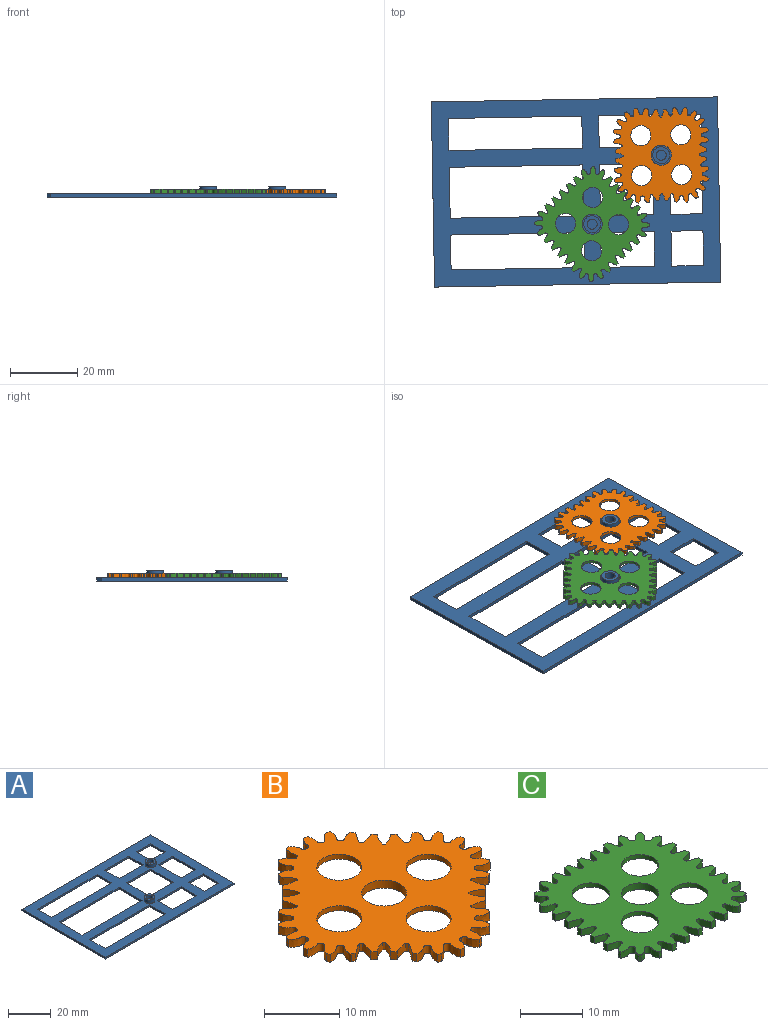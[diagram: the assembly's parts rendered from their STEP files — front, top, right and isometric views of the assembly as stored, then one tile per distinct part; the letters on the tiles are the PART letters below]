
ASSEMBLY  parts=3 mates=2
PART A: 50 faces, bbox 85x55x3 mm
  f0: plane 15.13x1mm, normal (-1,0,0), area 15.1mm2, adj f1,f39,f40,f41
  f1: plane 15.88x1mm, normal (0,1,0), area 15.9mm2, adj f0,f2,f40,f41
  f2: plane 15.13x1mm, normal (1,0,0), area 15.1mm2, adj f1,f39,f40,f41
  f3: plane 85x1mm, normal (0,-1,0), area 85mm2, adj f4,f30,f40,f41
  f4: plane 55x1mm, normal (1,0,0), area 55mm2, adj f3,f5,f40,f41
  f5: plane 85x1mm, normal (0,1,0), area 85mm2, adj f4,f30,f40,f41
  f6: plane 9.5x1mm, normal (0,-1,0), area 9.5mm2, adj f7,f31,f40,f41
  f7: plane 10.37x1mm, normal (-1,0,0), area 10.4mm2, adj f6,f8,f40,f41
  f8: plane 9.5x1mm, normal (0,1,0), area 9.5mm2, adj f7,f31,f40,f41
  f9: plane 39.62x1mm, normal (0,1,0), area 39.6mm2, adj f10,f32,f40,f41
  f10: plane 9.5x1mm, normal (1,0,0), area 9.5mm2, adj f9,f11,f40,f41
  f11: plane 39.62x1mm, normal (0,-1,0), area 39.6mm2, adj f10,f32,f40,f41
  f12: plane 39.62x1mm, normal (0,1,0), area 39.6mm2, adj f13,f33,f40,f41
  f13: plane 15.13x1mm, normal (1,0,0), area 15.1mm2, adj f12,f14,f40,f41
  f14: plane 39.62x1mm, normal (0,-1,0), area 39.6mm2, adj f13,f33,f40,f41
  f15: plane 10.37x1mm, normal (-1,0,0), area 10.4mm2, adj f16,f34,f40,f41
  f16: plane 39.62x1mm, normal (0,1,0), area 39.6mm2, adj f15,f17,f40,f41
  f17: plane 10.37x1mm, normal (1,0,0), area 10.4mm2, adj f16,f34,f40,f41
  f18: plane 10.37x1mm, normal (-1,0,0), area 10.4mm2, adj f19,f35,f40,f41
  f19: plane 15.88x1mm, normal (0,1,0), area 15.9mm2, adj f18,f20,f40,f41
  f20: plane 10.37x1mm, normal (1,0,0), area 10.4mm2, adj f19,f35,f40,f41
  f21: plane 15.13x1mm, normal (-1,0,0), area 15.1mm2, adj f22,f36,f40,f41
  f22: plane 9.5x1mm, normal (0,1,0), area 9.5mm2, adj f21,f23,f40,f41
  f23: plane 15.13x1mm, normal (1,0,0), area 15.1mm2, adj f22,f36,f40,f41
  f24: plane 9.5x1mm, normal (-1,0,0), area 9.5mm2, adj f25,f37,f40,f41
  f25: plane 9.5x1mm, normal (0,1,0), area 9.5mm2, adj f24,f26,f40,f41
  f26: plane 9.5x1mm, normal (1,0,0), area 9.5mm2, adj f25,f37,f40,f41
  f27: plane 15.88x1mm, normal (0,-1,0), area 15.9mm2, adj f28,f38,f40,f41
  f28: plane 9.5x1mm, normal (-1,0,0), area 9.5mm2, adj f27,f29,f40,f41
  f29: plane 15.88x1mm, normal (0,1,0), area 15.9mm2, adj f28,f38,f40,f41
  f30: plane 55x1mm, normal (-1,0,0), area 55mm2, adj f3,f5,f40,f41
  f31: plane 10.37x1mm, normal (1,0,0), area 10.4mm2, adj f6,f8,f40,f41
  f32: plane 9.5x1mm, normal (-1,0,0), area 9.5mm2, adj f9,f11,f40,f41
  f33: plane 15.13x1mm, normal (-1,0,0), area 15.1mm2, adj f12,f14,f40,f41
  f34: plane 39.62x1mm, normal (0,-1,0), area 39.6mm2, adj f15,f17,f40,f41
  f35: plane 15.88x1mm, normal (0,-1,0), area 15.9mm2, adj f18,f20,f40,f41
  f36: plane 9.5x1mm, normal (0,-1,0), area 9.5mm2, adj f21,f23,f40,f41
  f37: plane 9.5x1mm, normal (0,-1,0), area 9.5mm2, adj f24,f26,f40,f41
  f38: plane 9.5x1mm, normal (1,0,0), area 9.5mm2, adj f27,f29,f40,f41
  f39: plane 15.88x1mm, normal (0,-1,0), area 15.9mm2, adj f0,f2,f40,f41
  f40: plane 85x55mm, normal (0,0,1), area 2360.7mm2, adj f0,f1,f2,f3,f4,f5,f6,f7
  f41: plane 85x55mm, normal (0,0,-1), area 2400mm2, adj f0,f1,f2,f3,f4,f5,f6,f7
  f42: cylinder r=1.5mm len=3mm, axis (0,0,-1), area 18.8mm2, adj f44,f45
  f43: cylinder r=2.5mm len=5mm, axis (0,0,-1), area 31.4mm2, adj f40,f44
  f44: plane 5x5mm, normal (0,0,1), area 12.6mm2, adj f42,f43
  f45: plane 3x3mm, normal (0,0,1), area 7.1mm2, adj f42
  f46: cylinder r=1.5mm len=3mm, axis (0,0,-1), area 18.8mm2, adj f48,f49
  f47: cylinder r=2.5mm len=5mm, axis (0,0,-1), area 31.4mm2, adj f40,f48
  f48: plane 5x5mm, normal (0,0,1), area 12.6mm2, adj f46,f47
  f49: plane 3x3mm, normal (0,0,1), area 7.1mm2, adj f46
PART B: 119 faces, bbox 33.1x33.1x1.5 mm
  f0: extruded ~2.01x1.38mm, area 3.4mm2, adj f1,f91,f115,f117
  f1: extruded ~2.01x1.38mm, area 3.4mm2, adj f0,f2,f115,f117
  f2: cylinder r=8.26mm len=1.3mm, axis (0,0,-1), area 0.8mm2, adj f1,f3,f115,f117
  f3: extruded ~2.53x2.44mm, area 6.7mm2, adj f2,f4,f115,f117
  f4: cylinder r=8.26mm len=1.3mm, axis (0,0,-1), area 0.7mm2, adj f3,f5,f115,f117
  f5: extruded ~2.57x2.56mm, area 6.8mm2, adj f4,f6,f115,f117
  f6: cylinder r=8.26mm len=1.3mm, axis (0,0,-1), area 0.8mm2, adj f5,f7,f115,f117
  f7: extruded ~1.99x1.3mm, area 3.1mm2, adj f6,f8,f115,f117
  f8: cylinder r=16.96mm len=1.3mm, axis (0,0,-1), area 0.5mm2, adj f7,f9,f115,f117
  f9: extruded ~2.22x1.3mm, area 3mm2, adj f8,f10,f115,f117
  f10: cylinder r=14.84mm len=1.3mm, axis (0,0,-1), area 1.1mm2, adj f9,f11,f115,f117
  f11: extruded ~2.05x1.3mm, area 3mm2, adj f10,f12,f115,f117
  f12: cylinder r=16.96mm len=1.3mm, axis (0,0,-1), area 0.4mm2, adj f11,f13,f115,f117
  f13: extruded ~2.05x1.3mm, area 3mm2, adj f12,f14,f115,f117
  f14: cylinder r=14.84mm len=1.3mm, axis (0,0,-1), area 1.1mm2, adj f13,f15,f115,f117
  f15: extruded ~2.22x1.3mm, area 3mm2, adj f14,f16,f115,f117
  f16: cylinder r=16.96mm len=1.3mm, axis (0,0,-1), area 0.5mm2, adj f15,f17,f115,f117
  f17: extruded ~1.99x1.3mm, area 3.1mm2, adj f16,f18,f115,f117
  f18: cylinder r=8.26mm len=1.3mm, axis (0,0,-1), area 0.8mm2, adj f17,f19,f115,f117
  f19: extruded ~2.57x2.56mm, area 6.8mm2, adj f18,f20,f115,f117
  f20: cylinder r=8.26mm len=1.3mm, axis (0,0,-1), area 0.7mm2, adj f19,f21,f115,f117
  f21: extruded ~2.53x2.44mm, area 6.7mm2, adj f20,f22,f115,f117
  f22: cylinder r=8.26mm len=1.3mm, axis (0,0,-1), area 0.8mm2, adj f21,f23,f115,f117
  f23: extruded ~2.01x1.38mm, area 3.4mm2, adj f22,f24,f115,f117
  f24: extruded ~2.01x1.38mm, area 3.4mm2, adj f23,f25,f115,f117
  f25: cylinder r=8.26mm len=1.3mm, axis (0,0,-1), area 0.8mm2, adj f24,f26,f115,f117
  f26: extruded ~2.53x2.44mm, area 6.7mm2, adj f25,f27,f115,f117
  f27: cylinder r=8.26mm len=1.3mm, axis (0,0,-1), area 0.7mm2, adj f26,f28,f115,f117
  f28: extruded ~2.57x2.56mm, area 6.8mm2, adj f27,f29,f115,f117
  f29: cylinder r=8.26mm len=1.3mm, axis (0,0,-1), area 0.8mm2, adj f28,f30,f115,f117
  f30: extruded ~1.99x1.3mm, area 3.1mm2, adj f29,f31,f115,f117
  f31: cylinder r=16.96mm len=1.3mm, axis (0,0,-1), area 0.5mm2, adj f30,f32,f115,f117
  f32: extruded ~2.22x1.3mm, area 3mm2, adj f31,f33,f115,f117
  f33: cylinder r=14.84mm len=1.3mm, axis (0,0,-1), area 1.1mm2, adj f32,f34,f115,f117
  f34: extruded ~2.05x1.3mm, area 3mm2, adj f33,f35,f115,f117
  f35: cylinder r=16.96mm len=1.3mm, axis (0,0,-1), area 0.4mm2, adj f34,f36,f115,f117
  f36: extruded ~2.05x1.3mm, area 3mm2, adj f35,f37,f115,f117
  f37: cylinder r=14.84mm len=1.3mm, axis (0,0,-1), area 1.1mm2, adj f36,f38,f115,f117
  f38: extruded ~2.22x1.3mm, area 3mm2, adj f37,f39,f115,f117
  f39: cylinder r=16.96mm len=1.3mm, axis (0,0,-1), area 0.5mm2, adj f38,f40,f115,f117
  f40: extruded ~1.99x1.3mm, area 3.1mm2, adj f39,f41,f115,f117
  f41: cylinder r=8.26mm len=1.3mm, axis (0,0,-1), area 0.8mm2, adj f40,f42,f115,f117
  f42: extruded ~2.57x2.56mm, area 6.8mm2, adj f41,f43,f115,f117
  f43: cylinder r=8.26mm len=1.3mm, axis (0,0,-1), area 0.7mm2, adj f42,f44,f115,f117
  f44: extruded ~2.53x2.44mm, area 6.7mm2, adj f43,f45,f115,f117
  f45: cylinder r=8.26mm len=1.3mm, axis (0,0,-1), area 0.8mm2, adj f44,f46,f115,f117
  f46: extruded ~2.01x1.38mm, area 3.4mm2, adj f45,f47,f115,f117
  f47: extruded ~2.01x1.38mm, area 3.4mm2, adj f46,f48,f115,f117
  f48: cylinder r=8.26mm len=1.3mm, axis (0,0,-1), area 0.8mm2, adj f47,f49,f115,f117
  f49: extruded ~2.53x2.44mm, area 6.7mm2, adj f48,f50,f115,f117
  f50: cylinder r=8.26mm len=1.3mm, axis (0,0,-1), area 0.7mm2, adj f49,f51,f115,f117
  f51: extruded ~2.57x2.56mm, area 6.8mm2, adj f50,f52,f115,f117
  f52: cylinder r=8.26mm len=1.3mm, axis (0,0,-1), area 0.8mm2, adj f51,f53,f115,f117
  f53: extruded ~1.99x1.3mm, area 3.1mm2, adj f52,f54,f115,f117
  f54: cylinder r=16.96mm len=1.3mm, axis (0,0,-1), area 0.5mm2, adj f53,f55,f115,f117
  f55: extruded ~2.22x1.3mm, area 3mm2, adj f54,f56,f115,f117
  f56: cylinder r=14.84mm len=1.3mm, axis (0,0,-1), area 1.1mm2, adj f55,f57,f115,f117
  f57: extruded ~2.05x1.3mm, area 3mm2, adj f56,f58,f115,f117
  f58: cylinder r=16.96mm len=1.3mm, axis (0,0,-1), area 0.4mm2, adj f57,f59,f115,f117
  f59: extruded ~2.05x1.3mm, area 3mm2, adj f58,f60,f115,f117
  f60: cylinder r=14.84mm len=1.3mm, axis (0,0,-1), area 1.1mm2, adj f59,f61,f115,f117
  f61: extruded ~2.22x1.3mm, area 3mm2, adj f60,f62,f115,f117
  f62: cylinder r=16.96mm len=1.3mm, axis (0,0,-1), area 0.5mm2, adj f61,f63,f115,f117
  f63: extruded ~1.99x1.3mm, area 3.1mm2, adj f62,f64,f115,f117
  f64: cylinder r=8.26mm len=1.3mm, axis (0,0,-1), area 0.8mm2, adj f63,f65,f115,f117
  f65: extruded ~2.57x2.56mm, area 6.8mm2, adj f64,f66,f115,f117
  f66: cylinder r=8.26mm len=1.3mm, axis (0,0,-1), area 0.7mm2, adj f65,f67,f115,f117
  f67: extruded ~2.53x2.44mm, area 6.7mm2, adj f66,f68,f115,f117
  f68: cylinder r=8.26mm len=1.3mm, axis (0,0,-1), area 0.8mm2, adj f67,f69,f115,f117
  f69: extruded ~2.01x1.38mm, area 3.4mm2, adj f68,f70,f115,f117
  f70: extruded ~2.01x1.38mm, area 3.4mm2, adj f69,f71,f115,f117
  f71: cylinder r=8.26mm len=1.3mm, axis (0,0,-1), area 0.8mm2, adj f70,f72,f115,f117
  f72: extruded ~2.53x2.44mm, area 6.7mm2, adj f71,f73,f115,f117
  f73: cylinder r=8.26mm len=1.3mm, axis (0,0,-1), area 0.7mm2, adj f72,f74,f115,f117
  f74: extruded ~2.57x2.56mm, area 6.8mm2, adj f73,f75,f115,f117
  f75: cylinder r=8.26mm len=1.3mm, axis (0,0,-1), area 0.8mm2, adj f74,f76,f115,f117
  f76: extruded ~1.99x1.3mm, area 3.1mm2, adj f75,f77,f115,f117
  f77: cylinder r=16.96mm len=1.3mm, axis (0,0,-1), area 0.5mm2, adj f76,f78,f115,f117
  f78: extruded ~2.22x1.3mm, area 3mm2, adj f77,f79,f115,f117
  f79: cylinder r=14.84mm len=1.3mm, axis (0,0,-1), area 1.1mm2, adj f78,f80,f115,f117
  f80: extruded ~2.05x1.3mm, area 3mm2, adj f79,f81,f115,f117
  f81: cylinder r=16.96mm len=1.3mm, axis (0,0,-1), area 0.4mm2, adj f80,f82,f115,f117
  f82: extruded ~2.05x1.3mm, area 3mm2, adj f81,f83,f115,f117
  f83: cylinder r=14.84mm len=1.3mm, axis (0,0,-1), area 1.1mm2, adj f82,f84,f115,f117
  f84: extruded ~2.22x1.3mm, area 3mm2, adj f83,f85,f115,f117
  f85: cylinder r=16.96mm len=1.3mm, axis (0,0,-1), area 0.5mm2, adj f84,f86,f115,f117
  f86: extruded ~1.99x1.3mm, area 3.1mm2, adj f85,f87,f115,f117
  f87: cylinder r=8.26mm len=1.3mm, axis (0,0,-1), area 0.8mm2, adj f86,f88,f115,f117
  f88: extruded ~2.57x2.56mm, area 6.8mm2, adj f87,f89,f115,f117
  f89: cylinder r=8.26mm len=1.3mm, axis (0,0,-1), area 0.7mm2, adj f88,f90,f115,f117
  f90: extruded ~2.53x2.44mm, area 6.7mm2, adj f89,f91,f115,f117
  f91: cylinder r=8.26mm len=1.3mm, axis (0,0,-1), area 0.8mm2, adj f0,f90,f115,f117
  f92: cylinder r=2.8mm len=3.96mm, axis (0,0,1), area 0.4mm2, adj f93,f99,f110,f117
  f93: plane 10.18x10.18mm, normal (0.71,-0.71,0), area 1.4mm2, adj f92,f94,f112,f117
  f94: cylinder r=2.8mm len=3.96mm, axis (0,0,1), area 0.4mm2, adj f93,f95,f113,f117
  f95: plane 10.18x10.18mm, normal (-0.71,-0.71,0), area 1.4mm2, adj f94,f96,f111,f117
  f96: cylinder r=2.8mm len=3.96mm, axis (0,0,1), area 0.4mm2, adj f95,f97,f109,f117
  f97: plane 10.18x10.18mm, normal (-0.71,0.71,0), area 1.4mm2, adj f96,f98,f107,f117
  f98: cylinder r=2.8mm len=3.96mm, axis (0,0,1), area 0.4mm2, adj f97,f99,f106,f117
  f99: plane 10.18x10.18mm, normal (0.71,0.71,0), area 1.4mm2, adj f92,f98,f108,f117
  f100: cylinder r=4mm len=8mm, axis (0,0,1), area 2.5mm2, adj f114,f116
  f101: cylinder r=3mm len=6mm, axis (0,0,1), area 15.1mm2, adj f105,f115
  f102: cylinder r=3mm len=6mm, axis (0,0,1), area 15.1mm2, adj f105,f115
  f103: cylinder r=3mm len=6mm, axis (0,0,1), area 15.1mm2, adj f105,f115
  f104: cylinder r=3mm len=6mm, axis (0,0,1), area 15.1mm2, adj f105,f115
  f105: plane 25.16x25.16mm, normal (0,0,-1), area 189.8mm2, adj f101,f102,f103,f104,f106,f107,f108,f109
  f106: torus R=2.4mm, axis (0,0,1), area 2.6mm2, adj f98,f105,f107,f108
  f107: cylinder r=0.4mm len=10.47mm, axis (-0.71,-0.71,0), area 9mm2, adj f97,f105,f106,f109
  f108: cylinder r=0.4mm len=10.47mm, axis (-0.71,0.71,0), area 9mm2, adj f99,f105,f106,f110
  f109: torus R=2.4mm, axis (0,0,1), area 2.6mm2, adj f96,f105,f107,f111
  f110: torus R=2.4mm, axis (0,0,1), area 2.6mm2, adj f92,f105,f108,f112
  f111: cylinder r=0.4mm len=10.47mm, axis (0.71,-0.71,0), area 9mm2, adj f95,f105,f109,f113
  f112: cylinder r=0.4mm len=10.47mm, axis (0.71,0.71,0), area 9mm2, adj f93,f105,f110,f113
  f113: torus R=2.4mm, axis (0,0,1), area 2.6mm2, adj f94,f105,f111,f112
  f114: torus R=4.4mm, axis (0,0,1), area 16.4mm2, adj f100,f105
  f115: plane 33.09x33.09mm, normal (0,0,1), area 489mm2, adj f0,f1,f2,f3,f4,f5,f6,f7
  f116: plane 8x8mm, normal (0,0,-1), area 22mm2, adj f100,f118
  f117: plane 33.09x33.09mm, normal (0,0,-1), area 237.1mm2, adj f0,f1,f2,f3,f4,f5,f6,f7
  f118: cylinder r=3mm len=6mm, axis (0,0,1), area 24.5mm2, adj f115,f116
PART C: 91 faces, bbox 27.5x27.5x1.5 mm
  f0: extruded ~2.65x2.45mm, area 6.8mm2, adj f1,f63,f87,f89
  f1: cylinder r=5.76mm len=1.3mm, axis (0,0,-1), area 0.7mm2, adj f0,f2,f87,f89
  f2: extruded ~2.51x2.16mm, area 6.7mm2, adj f1,f3,f87,f89
  f3: plane 1.3x0.74mm, normal (0,1,0), area 1mm2, adj f2,f4,f87,f89
  f4: extruded ~2.18x2.13mm, area 6.5mm2, adj f3,f5,f87,f89
  f5: plane 1.3x0.78mm, normal (0,1,0), area 1mm2, adj f4,f6,f87,f89
  f6: extruded ~2.17x2.14mm, area 6.5mm2, adj f5,f7,f87,f89
  f7: plane 1.3x0.77mm, normal (0,1,0), area 1mm2, adj f6,f8,f87,f89
  f8: extruded ~2.17x2.14mm, area 6.5mm2, adj f7,f9,f87,f89
  f9: plane 1.3x0.78mm, normal (0,1,0), area 1mm2, adj f8,f10,f87,f89
  f10: extruded ~2.18x2.13mm, area 6.5mm2, adj f9,f11,f87,f89
  f11: plane 1.3x0.74mm, normal (0,1,0), area 1mm2, adj f10,f12,f87,f89
  f12: extruded ~2.51x2.16mm, area 6.7mm2, adj f11,f13,f87,f89
  f13: cylinder r=5.76mm len=1.3mm, axis (0,0,-1), area 0.7mm2, adj f12,f14,f87,f89
  f14: extruded ~2.65x2.45mm, area 6.8mm2, adj f13,f15,f87,f89
  f15: cylinder r=5.76mm len=1.3mm, axis (0,0,-1), area 0.5mm2, adj f14,f16,f87,f89
  f16: extruded ~2.65x2.45mm, area 6.8mm2, adj f15,f17,f87,f89
  f17: cylinder r=5.76mm len=1.3mm, axis (0,0,-1), area 0.7mm2, adj f16,f18,f87,f89
  f18: extruded ~2.51x2.16mm, area 6.7mm2, adj f17,f19,f87,f89
  f19: plane 1.3x0.74mm, normal (-1,0,0), area 1mm2, adj f18,f20,f87,f89
  f20: extruded ~2.18x2.13mm, area 6.5mm2, adj f19,f21,f87,f89
  f21: plane 1.3x0.78mm, normal (-1,0,0), area 1mm2, adj f20,f22,f87,f89
  f22: extruded ~2.17x2.14mm, area 6.5mm2, adj f21,f23,f87,f89
  f23: plane 1.3x0.77mm, normal (-1,0,0), area 1mm2, adj f22,f24,f87,f89
  f24: extruded ~2.17x2.14mm, area 6.5mm2, adj f23,f25,f87,f89
  f25: plane 1.3x0.78mm, normal (-1,0,0), area 1mm2, adj f24,f26,f87,f89
  f26: extruded ~2.18x2.13mm, area 6.5mm2, adj f25,f27,f87,f89
  f27: plane 1.3x0.74mm, normal (-1,0,0), area 1mm2, adj f26,f28,f87,f89
  f28: extruded ~2.51x2.16mm, area 6.7mm2, adj f27,f29,f87,f89
  f29: cylinder r=5.76mm len=1.3mm, axis (0,0,-1), area 0.7mm2, adj f28,f30,f87,f89
  f30: extruded ~2.65x2.45mm, area 6.8mm2, adj f29,f31,f87,f89
  f31: cylinder r=5.76mm len=1.3mm, axis (0,0,-1), area 0.5mm2, adj f30,f32,f87,f89
  f32: extruded ~2.65x2.45mm, area 6.8mm2, adj f31,f33,f87,f89
  f33: cylinder r=5.76mm len=1.3mm, axis (0,0,-1), area 0.7mm2, adj f32,f34,f87,f89
  f34: extruded ~2.51x2.16mm, area 6.7mm2, adj f33,f35,f87,f89
  f35: plane 1.3x0.74mm, normal (0,-1,0), area 1mm2, adj f34,f36,f87,f89
  f36: extruded ~2.18x2.13mm, area 6.5mm2, adj f35,f37,f87,f89
  f37: plane 1.3x0.78mm, normal (0,-1,0), area 1mm2, adj f36,f38,f87,f89
  f38: extruded ~2.17x2.14mm, area 6.5mm2, adj f37,f39,f87,f89
  f39: plane 1.3x0.77mm, normal (0,-1,0), area 1mm2, adj f38,f40,f87,f89
  f40: extruded ~2.17x2.14mm, area 6.5mm2, adj f39,f41,f87,f89
  f41: plane 1.3x0.78mm, normal (0,-1,0), area 1mm2, adj f40,f42,f87,f89
  f42: extruded ~2.18x2.13mm, area 6.5mm2, adj f41,f43,f87,f89
  f43: plane 1.3x0.74mm, normal (0,-1,0), area 1mm2, adj f42,f44,f87,f89
  f44: extruded ~2.51x2.16mm, area 6.7mm2, adj f43,f45,f87,f89
  f45: cylinder r=5.76mm len=1.3mm, axis (0,0,-1), area 0.7mm2, adj f44,f46,f87,f89
  f46: extruded ~2.65x2.45mm, area 6.8mm2, adj f45,f47,f87,f89
  f47: cylinder r=5.76mm len=1.3mm, axis (0,0,-1), area 0.5mm2, adj f46,f48,f87,f89
  f48: extruded ~2.65x2.45mm, area 6.8mm2, adj f47,f49,f87,f89
  f49: cylinder r=5.76mm len=1.3mm, axis (0,0,-1), area 0.7mm2, adj f48,f50,f87,f89
  f50: extruded ~2.51x2.16mm, area 6.7mm2, adj f49,f51,f87,f89
  f51: plane 1.3x0.74mm, normal (1,0,0), area 1mm2, adj f50,f52,f87,f89
  f52: extruded ~2.18x2.13mm, area 6.5mm2, adj f51,f53,f87,f89
  f53: plane 1.3x0.78mm, normal (1,0,0), area 1mm2, adj f52,f54,f87,f89
  f54: extruded ~2.17x2.14mm, area 6.5mm2, adj f53,f55,f87,f89
  f55: plane 1.3x0.77mm, normal (1,0,0), area 1mm2, adj f54,f56,f87,f89
  f56: extruded ~2.17x2.14mm, area 6.5mm2, adj f55,f57,f87,f89
  f57: plane 1.3x0.78mm, normal (1,0,0), area 1mm2, adj f56,f58,f87,f89
  f58: extruded ~2.18x2.13mm, area 6.5mm2, adj f57,f59,f87,f89
  f59: plane 1.3x0.74mm, normal (1,0,0), area 1mm2, adj f58,f60,f87,f89
  f60: extruded ~2.51x2.16mm, area 6.7mm2, adj f59,f61,f87,f89
  f61: cylinder r=5.76mm len=1.3mm, axis (0,0,-1), area 0.7mm2, adj f60,f62,f87,f89
  f62: extruded ~2.65x2.45mm, area 6.8mm2, adj f61,f63,f87,f89
  f63: cylinder r=5.76mm len=1.3mm, axis (0,0,-1), area 0.5mm2, adj f0,f62,f87,f89
  f64: cylinder r=2.8mm len=2.8mm, axis (0,0,1), area 0.4mm2, adj f65,f71,f82,f89
  f65: plane 14.4x0.1mm, normal (1,0,0), area 1.4mm2, adj f64,f66,f84,f89
  f66: cylinder r=2.8mm len=2.8mm, axis (0,0,1), area 0.4mm2, adj f65,f67,f85,f89
  f67: plane 14.4x0.1mm, normal (0,-1,0), area 1.4mm2, adj f66,f68,f83,f89
  f68: cylinder r=2.8mm len=2.8mm, axis (0,0,1), area 0.4mm2, adj f67,f69,f81,f89
  f69: plane 14.4x0.1mm, normal (-1,0,0), area 1.4mm2, adj f68,f70,f79,f89
  f70: cylinder r=2.8mm len=2.8mm, axis (0,0,1), area 0.4mm2, adj f69,f71,f78,f89
  f71: plane 14.4x0.1mm, normal (0,1,0), area 1.4mm2, adj f64,f70,f80,f89
  f72: cylinder r=4mm len=8mm, axis (0,0,1), area 2.5mm2, adj f86,f88
  f73: cylinder r=3mm len=6mm, axis (0,0,1), area 15.1mm2, adj f77,f87
  f74: cylinder r=3mm len=6mm, axis (0,0,1), area 15.1mm2, adj f77,f87
  f75: cylinder r=3mm len=6mm, axis (0,0,1), area 15.1mm2, adj f77,f87
  f76: cylinder r=3mm len=6mm, axis (0,0,1), area 15.1mm2, adj f77,f87
  f77: plane 19.2x19.2mm, normal (0,0,-1), area 189.8mm2, adj f73,f74,f75,f76,f78,f79,f80,f81
  f78: torus R=2.4mm, axis (0,0,1), area 2.6mm2, adj f70,f77,f79,f80
  f79: cylinder r=0.4mm len=14.4mm, axis (0,-1,0), area 9mm2, adj f69,f77,f78,f81
  f80: cylinder r=0.4mm len=14.4mm, axis (-1,0,0), area 9mm2, adj f71,f77,f78,f82
  f81: torus R=2.4mm, axis (0,0,1), area 2.6mm2, adj f68,f77,f79,f83
  f82: torus R=2.4mm, axis (0,0,1), area 2.6mm2, adj f64,f77,f80,f84
  f83: cylinder r=0.4mm len=14.4mm, axis (1,0,0), area 9mm2, adj f67,f77,f81,f85
  f84: cylinder r=0.4mm len=14.4mm, axis (0,1,0), area 9mm2, adj f65,f77,f82,f85
  f85: torus R=2.4mm, axis (0,0,1), area 2.6mm2, adj f66,f77,f83,f84
  f86: torus R=4.4mm, axis (0,0,1), area 16.4mm2, adj f72,f77
  f87: plane 27.52x27.52mm, normal (0,0,1), area 489.5mm2, adj f0,f1,f2,f3,f4,f5,f6,f7
  f88: plane 8x8mm, normal (0,0,-1), area 22mm2, adj f72,f90
  f89: plane 27.52x27.52mm, normal (0,0,-1), area 237.6mm2, adj f0,f1,f2,f3,f4,f5,f6,f7
  f90: cylinder r=3mm len=6mm, axis (0,0,1), area 24.5mm2, adj f87,f88
PLACE A rot(axis=(0,0,1),1deg) t=(5.02,28.24,-1.3)mm
PLACE B rot(axis=(0,0,-1),44deg) t=(-138.79,36.94,1)mm
PLACE C rot(axis=(0,0,-1),46deg) t=(-170.47,26.88,1)mm
MATE revolute B.f100 <-> A.f42  axis (0,0,-1) through (30.34,39.18,-0.3)mm
MATE revolute C.f72 <-> A.f46  axis (0,0,-1) through (9.81,18.69,-0.3)mm
